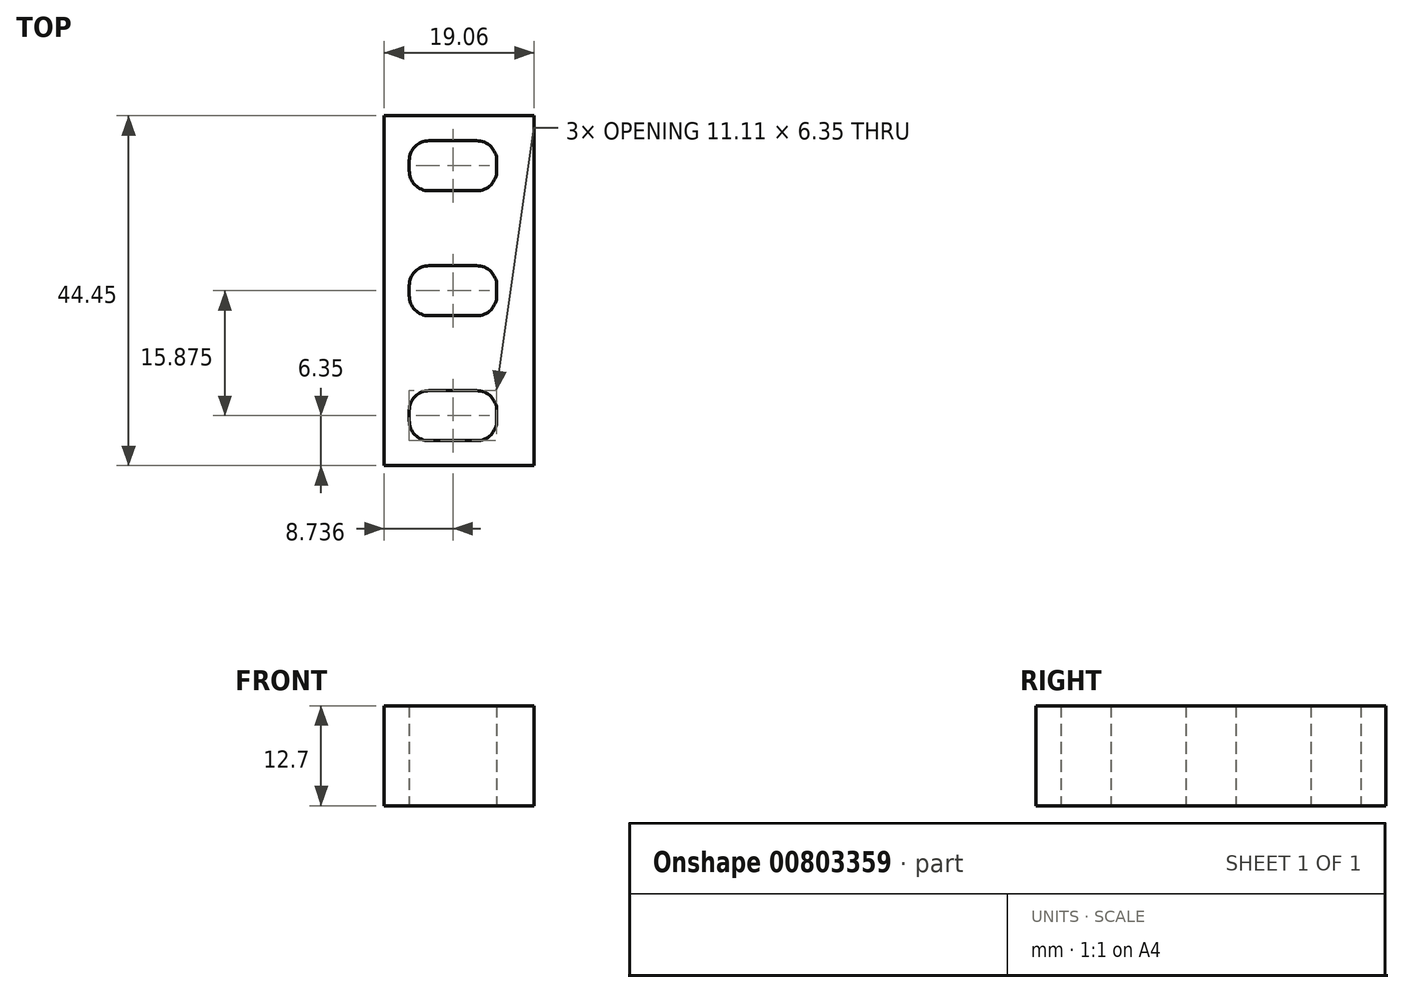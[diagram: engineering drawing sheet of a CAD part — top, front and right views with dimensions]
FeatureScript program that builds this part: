
annotation { "Feature Type Name" : "Feature", "Feature Type Description" : "" }
export const myFeature = defineFeature(function(context is Context, id is Id, definition is map)
    precondition{}
    {
        {
            var Q0;
            Q0=qCreatedBy(makeId("Top.planeOp"),FACE);
            var sketch = newSketch(context, id + "F0", { "sketchPlane" : qUnion([Q0])});
            skLineSegment(sketch, "E0.bottom", {"start": v(-9.53, 0) * mm, "end": v(9.53, 0) * mm});
            skLineSegment(sketch, "E0.top", {"start": v(-9.53, -44.45) * mm, "end": v(9.53, -44.45) * mm});
            skLineSegment(sketch, "E0.left", {"start": v(-9.53, 0) * mm, "end": v(-9.53, -44.45) * mm});
            skLineSegment(sketch, "E0.right", {"start": v(9.53, 0) * mm, "end": v(9.53, -44.45) * mm});
            skLineSegment(sketch, "E1.bottom", {"start": v(-3.8, -3.18) * mm, "end": v(2.22, -3.17) * mm});
            skLineSegment(sketch, "E1.top", {"start": v(-3.8, -9.53) * mm, "end": v(2.22, -9.53) * mm});
            skLineSegment(sketch, "E1.left", {"start": v(-6.35, -5.72) * mm, "end": v(-6.35, -6.99) * mm});
            skLineSegment(sketch, "E1.right", {"start": v(4.76, -5.71) * mm, "end": v(4.76, -6.98) * mm});
            skPoint(sketch, "E2.visualSharp", {"position": v(-6.35, -3.18) * mm});
            skArc(sketch, "E2.filletArc", {"start": v(-3.8, -3.18) * mm, "mid": v(-5.6, -3.92) * mm, "end": v(-6.35, -5.72) * mm});
            skPoint(sketch, "E3.visualSharp", {"position": v(-6.35, -9.53) * mm});
            skArc(sketch, "E3.filletArc", {"start": v(-6.35, -6.99) * mm, "mid": v(-5.6, -8.78) * mm, "end": v(-3.8, -9.53) * mm});
            skPoint(sketch, "E4.visualSharp", {"position": v(4.76, -3.17) * mm});
            skArc(sketch, "E4.filletArc", {"start": v(4.76, -5.71) * mm, "mid": v(4.02, -3.92) * mm, "end": v(2.22, -3.17) * mm});
            skPoint(sketch, "E5.visualSharp", {"position": v(4.76, -9.52) * mm});
            skArc(sketch, "E5.filletArc", {"start": v(2.22, -9.52) * mm, "mid": v(4.02, -8.78) * mm, "end": v(4.76, -6.98) * mm});
            skLineSegment(sketch, "E6.bottom", {"start": v(-3.8, -34.93) * mm, "end": v(2.22, -34.93) * mm});
            skLineSegment(sketch, "E6.top", {"start": v(-3.8, -41.28) * mm, "end": v(2.22, -41.28) * mm});
            skLineSegment(sketch, "E6.left", {"start": v(-6.35, -37.47) * mm, "end": v(-6.35, -38.74) * mm});
            skLineSegment(sketch, "E6.right", {"start": v(4.76, -37.47) * mm, "end": v(4.76, -38.74) * mm});
            skPoint(sketch, "E7.visualSharp", {"position": v(-6.35, -34.93) * mm});
            skArc(sketch, "E7.filletArc", {"start": v(-3.8, -34.93) * mm, "mid": v(-5.6, -35.67) * mm, "end": v(-6.35, -37.47) * mm});
            skPoint(sketch, "E8.visualSharp", {"position": v(-6.35, -41.28) * mm});
            skArc(sketch, "E8.filletArc", {"start": v(-6.35, -38.74) * mm, "mid": v(-5.6, -40.53) * mm, "end": v(-3.8, -41.28) * mm});
            skPoint(sketch, "E9.visualSharp", {"position": v(4.76, -41.28) * mm});
            skArc(sketch, "E9.filletArc", {"start": v(2.22, -41.28) * mm, "mid": v(4.02, -40.53) * mm, "end": v(4.76, -38.74) * mm});
            skPoint(sketch, "E10.visualSharp", {"position": v(4.76, -34.93) * mm});
            skArc(sketch, "E10.filletArc", {"start": v(4.76, -37.47) * mm, "mid": v(4.02, -35.67) * mm, "end": v(2.22, -34.93) * mm});
            skLineSegment(sketch, "E11.bottom", {"start": v(-3.8, -19.05) * mm, "end": v(2.22, -19.05) * mm});
            skLineSegment(sketch, "E11.top", {"start": v(-3.8, -25.4) * mm, "end": v(2.22, -25.4) * mm});
            skLineSegment(sketch, "E11.left", {"start": v(-6.35, -21.59) * mm, "end": v(-6.35, -22.86) * mm});
            skLineSegment(sketch, "E11.right", {"start": v(4.76, -21.59) * mm, "end": v(4.76, -22.86) * mm});
            skPoint(sketch, "E12.visualSharp", {"position": v(-6.35, -19.05) * mm});
            skArc(sketch, "E12.filletArc", {"start": v(-3.8, -19.05) * mm, "mid": v(-5.6, -19.8) * mm, "end": v(-6.35, -21.59) * mm});
            skPoint(sketch, "E13.visualSharp", {"position": v(-6.35, -25.4) * mm});
            skArc(sketch, "E13.filletArc", {"start": v(-6.35, -22.86) * mm, "mid": v(-5.6, -24.66) * mm, "end": v(-3.8, -25.4) * mm});
            skPoint(sketch, "E14.visualSharp", {"position": v(4.76, -25.4) * mm});
            skArc(sketch, "E14.filletArc", {"start": v(2.22, -25.4) * mm, "mid": v(4.02, -24.66) * mm, "end": v(4.76, -22.86) * mm});
            skPoint(sketch, "E15.visualSharp", {"position": v(4.76, -19.05) * mm});
            skArc(sketch, "E15.filletArc", {"start": v(4.76, -21.59) * mm, "mid": v(4.02, -19.8) * mm, "end": v(2.22, -19.05) * mm});
            skSolve(sketch);
        }
        {
            var Q0;
            Q0=makeQuery(id+"F0.imprint","IMPRINT",FACE,{"disambiguationData":[TD([[makeQuery(id+"F0.imprint","IMPRINT",EDGE,{"derivedFrom":sQuery(id+"F0.wireOp",EDGE,"E0.bottom")}),-1.0]])]});
            extrude(context, id + "F1", {"entities" : qUnion([Q0]), "depth" : 12.7 * mm, "offsetDistance" : 25.4 * mm});
        }
    });
